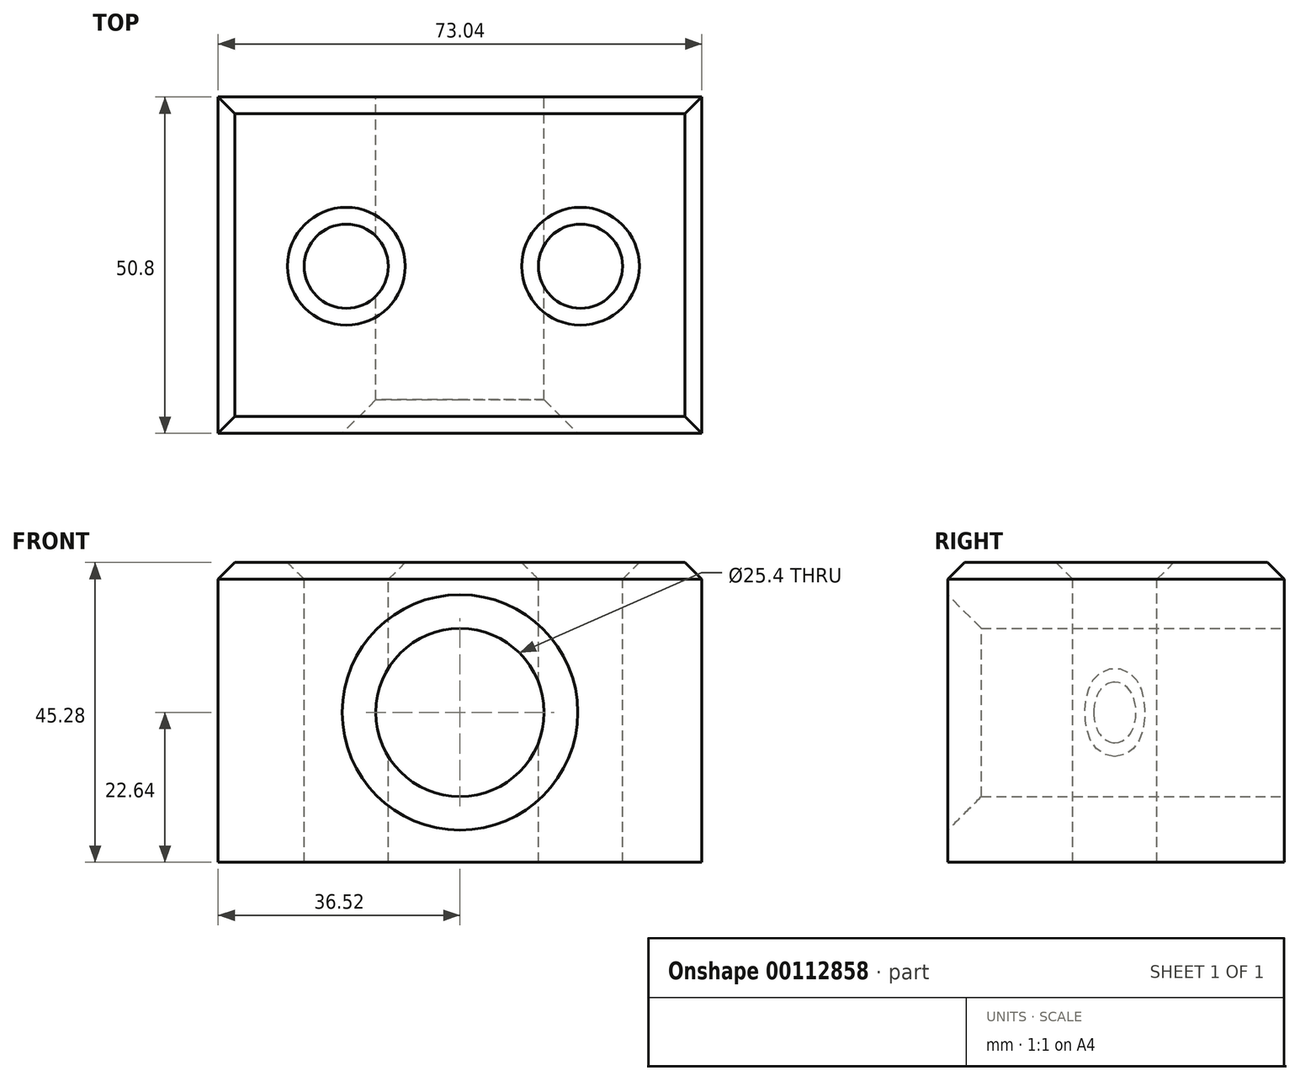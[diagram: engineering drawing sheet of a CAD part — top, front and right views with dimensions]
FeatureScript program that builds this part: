
annotation { "Feature Type Name" : "Feature", "Feature Type Description" : "" }
export const myFeature = defineFeature(function(context is Context, id is Id, definition is map)
    precondition{}
    {
        {
            var Q0;
            Q0=qCreatedBy(makeId("Front.planeOp"),FACE);
            var sketch = newSketch(context, id + "F0", { "sketchPlane" : qUnion([Q0])});
            skLineSegment(sketch, "E0.bottom", {"start": v(36.52, 22.64) * mm, "end": v(-36.52, 22.64) * mm});
            skLineSegment(sketch, "E0.top", {"start": v(36.52, -22.64) * mm, "end": v(-36.52, -22.64) * mm});
            skLineSegment(sketch, "E0.left", {"start": v(36.52, 22.64) * mm, "end": v(36.52, -22.64) * mm});
            skLineSegment(sketch, "E0.right", {"start": v(-36.52, 22.64) * mm, "end": v(-36.52, -22.64) * mm});
            skPoint(sketch, "E0.middle", {"position": v(0, 0) * mm});
            skCircle(sketch, "E1", {"center": v(0, 0) * mm, "radius": 12.7 * mm});
            skSolve(sketch);
        }
        {
            var Q0;
            Q0 = qSketchRegion(id + "F0", true);
            extrude(context, id + "F1", {"entities" : qUnion([Q0]), "depth" : 50.8 * mm});
        }
        {
            var Q0;
            Q0=makeQuery(id+"F1.opExtrude","SWEPT_FACE",FACE,{"disambiguationData":[OSD([sQuery(id+"F0.wireOp",EDGE,"E0.bottom")])]});
            var sketch = newSketch(context, id + "F2", { "sketchPlane" : qUnion([Q0])});
            skPoint(sketch, "E2", {"position": v(-17.16, -25.55) * mm});
            skPoint(sketch, "E3", {"position": v(18.2, -25.55) * mm});
            skSolve(sketch);
        }
        {
            var Q0;
            Q0=sQuery(id+"F2.wireOp",VERTEX,"E2");
            var Q1;
            Q1=sQuery(id+"F2.wireOp",VERTEX,"E3");
            var Q2;
            Q2=makeQuery(id+"F1.opExtrude","SWEPT_BODY",BODY,{"disambiguationData":[OSD([sQuery(id+"F0.wireOp",EDGE,"E0.bottom"),sQuery(id+"F0.wireOp",EDGE,"E0.top"),sQuery(id+"F0.wireOp",EDGE,"E0.left"),sQuery(id+"F0.wireOp",EDGE,"E0.right"),sQuery(id+"F0.wireOp",EDGE,"E1")])]});
            hole(context, id + "F3", {"style" : HoleStyle.SIMPLE, "endStyle" : HoleEndStyle.THROUGH, "holeDiameter" : 12.7 * mm, "startFromSketch" : true, "locations" : qUnion([Q0, Q1]), "scope" : qUnion([Q2]), "isTappedThrough" : true});
        }
        {
            var Q0;
            Q0=makeQuery(id+"F1.opExtrude","CAP_EDGE",EDGE,{"disambiguationData":[OSD([sQuery(id+"F0.wireOp",EDGE,"E1")])],"isStart":false});
            chamfer(context, id + "F4", {"entities" : qUnion([Q0]), "width" : 5.08 * mm, "tangentPropagation" : true});
        }
        {
            var Q0;
            Q0=makeQuery(id+"F1.opExtrude","SWEPT_FACE",FACE,{"disambiguationData":[OSD([sQuery(id+"F0.wireOp",EDGE,"E0.bottom")])]});
            chamfer(context, id + "F5", {"entities" : qUnion([Q0]), "width" : 2.54 * mm, "tangentPropagation" : true});
        }
    });
